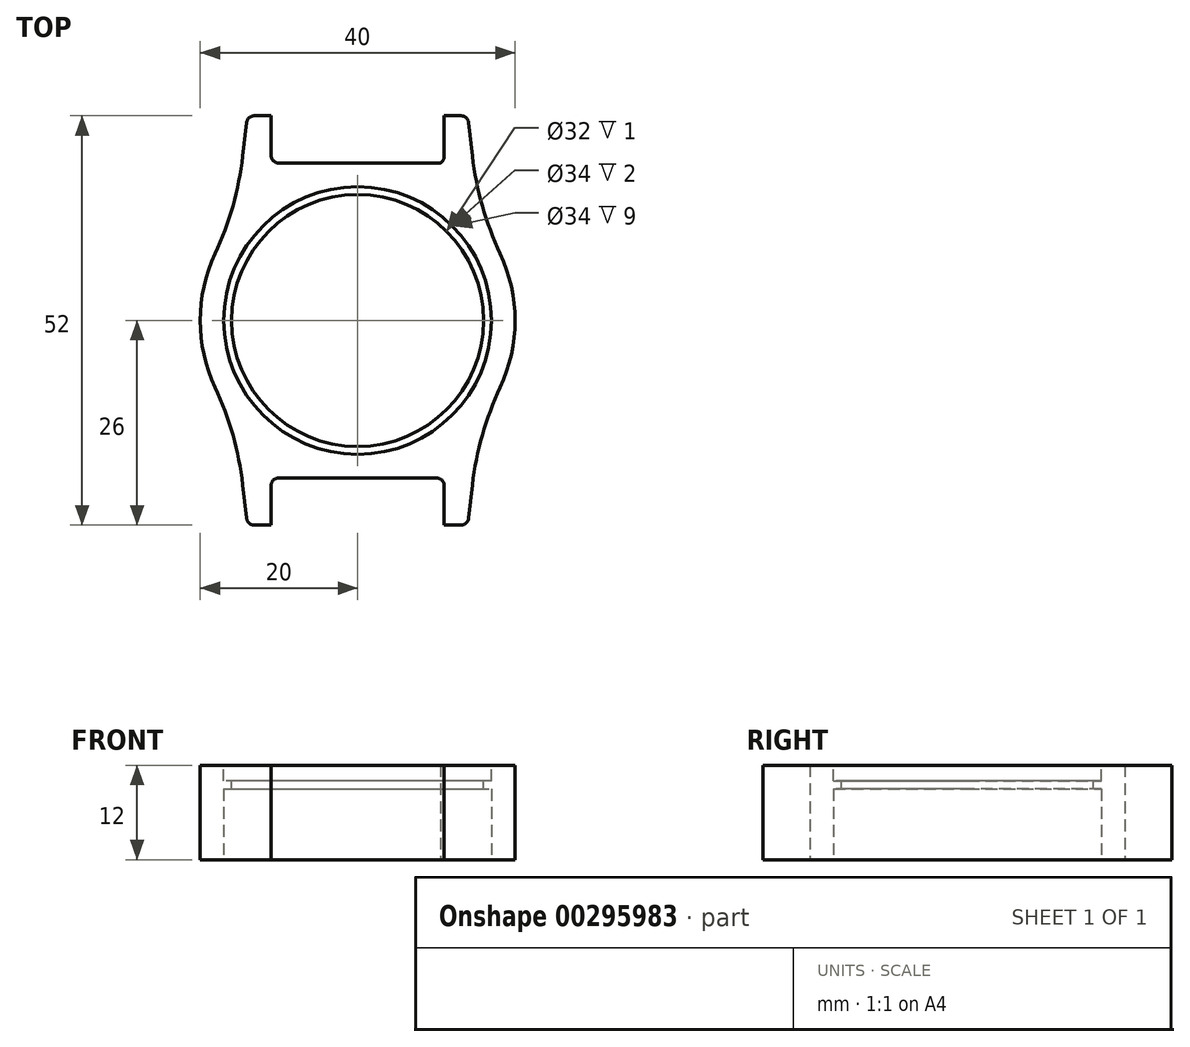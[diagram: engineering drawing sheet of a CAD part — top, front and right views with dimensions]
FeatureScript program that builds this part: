
annotation { "Feature Type Name" : "Feature", "Feature Type Description" : "" }
export const myFeature = defineFeature(function(context is Context, id is Id, definition is map)
    precondition{}
    {
        {
            var Q0;
            Q0=qCreatedBy(makeId("Top.planeOp"),FACE);
            var sketch = newSketch(context, id + "F0", { "sketchPlane" : qUnion([Q0])});
            skLineSegment(sketch, "E0", {"start": v(0, 20) * mm, "end": v(10.54, 20) * mm});
            skLineSegment(sketch, "E1", {"start": v(0, -20) * mm, "end": v(10, -20) * mm});
            skLineSegment(sketch, "E2", {"start": v(0, 20) * mm, "end": v(-10, 20) * mm});
            skLineSegment(sketch, "E3", {"start": v(0, -20) * mm, "end": v(-10, -20) * mm});
            skLineSegment(sketch, "E4", {"start": v(-11, 21) * mm, "end": v(-11, 26) * mm});
            skLineSegment(sketch, "E5", {"start": v(11, 20.84) * mm, "end": v(11, 26) * mm});
            skLineSegment(sketch, "E6", {"start": v(-11, -21) * mm, "end": v(-11, -26) * mm});
            skLineSegment(sketch, "E7", {"start": v(11, -21) * mm, "end": v(11, -26) * mm});
            skLineSegment(sketch, "E8", {"start": v(11, 26) * mm, "end": v(13.1, 26) * mm});
            skLineSegment(sketch, "E9", {"start": v(-11, 26) * mm, "end": v(-13.1, 26) * mm});
            skLineSegment(sketch, "E10", {"start": v(11, -26) * mm, "end": v(13.1, -26) * mm});
            skLineSegment(sketch, "E11", {"start": v(-11, -26) * mm, "end": v(-13.1, -26) * mm});
            skPoint(sketch, "E12.visualSharp", {"position": v(-11, 20) * mm});
            skArc(sketch, "E12.filletArc", {"start": v(-11, 21) * mm, "mid": v(-10.7, 20.3) * mm, "end": v(-10, 20) * mm});
            skPoint(sketch, "E13.visualSharp", {"position": v(11, 20) * mm});
            skArc(sketch, "E13.filletArc", {"start": v(10.54, 20) * mm, "mid": v(10.88, 20.36) * mm, "end": v(11, 20.84) * mm});
            skPoint(sketch, "E14.visualSharp", {"position": v(-11, -20) * mm});
            skArc(sketch, "E14.filletArc", {"start": v(-10, -20) * mm, "mid": v(-10.7, -20.3) * mm, "end": v(-11, -21) * mm});
            skPoint(sketch, "E15.visualSharp", {"position": v(11, -20) * mm});
            skArc(sketch, "E15.filletArc", {"start": v(11, -21) * mm, "mid": v(10.7, -20.3) * mm, "end": v(10, -20) * mm});
            skArc(sketch, "E16", {"start": v(-18.1, 8.49) * mm, "mid": v(-20, 0) * mm, "end": v(-18.1, -8.49) * mm});
            skLineSegment(sketch, "E17", {"start": v(-14.1, -25.11) * mm, "end": v(-14.6, -20.88) * mm});
            skLineSegment(sketch, "E18", {"start": v(14.1, -25.11) * mm, "end": v(14.6, -20.88) * mm});
            skLineSegment(sketch, "E19", {"start": v(-14.1, 25.11) * mm, "end": v(-14.6, 20.88) * mm});
            skLineSegment(sketch, "E20", {"start": v(14.1, 25.11) * mm, "end": v(14.6, 20.88) * mm});
            skArc(sketch, "E21.trimOffspring", {"start": v(18.1, -8.49) * mm, "mid": v(20, 0) * mm, "end": v(18.1, 8.49) * mm});
            skPoint(sketch, "E22.visualSharp", {"position": v(-15.55, -12.58) * mm});
            skArc(sketch, "E22.filletArc", {"start": v(-14.6, -20.88) * mm, "mid": v(-15.85, -14.54) * mm, "end": v(-18.1, -8.49) * mm});
            skPoint(sketch, "E23.visualSharp", {"position": v(15.55, -12.58) * mm});
            skArc(sketch, "E23.filletArc", {"start": v(18.1, -8.49) * mm, "mid": v(15.85, -14.54) * mm, "end": v(14.6, -20.88) * mm});
            skPoint(sketch, "E24.visualSharp", {"position": v(15.55, 12.58) * mm});
            skArc(sketch, "E24.filletArc", {"start": v(14.6, 20.88) * mm, "mid": v(15.85, 14.54) * mm, "end": v(18.1, 8.49) * mm});
            skPoint(sketch, "E25.visualSharp", {"position": v(-15.55, 12.58) * mm});
            skArc(sketch, "E25.filletArc", {"start": v(-18.1, 8.49) * mm, "mid": v(-15.85, 14.54) * mm, "end": v(-14.6, 20.88) * mm});
            skPoint(sketch, "E26.visualSharp", {"position": v(-14, 26) * mm});
            skArc(sketch, "E26.filletArc", {"start": v(-13.1, 26) * mm, "mid": v(-13.77, 25.75) * mm, "end": v(-14.1, 25.11) * mm});
            skPoint(sketch, "E27.visualSharp", {"position": v(14, 26) * mm});
            skArc(sketch, "E27.filletArc", {"start": v(14.1, 25.11) * mm, "mid": v(13.77, 25.75) * mm, "end": v(13.1, 26) * mm});
            skPoint(sketch, "E28.visualSharp", {"position": v(14, -26) * mm});
            skArc(sketch, "E28.filletArc", {"start": v(13.1, -26) * mm, "mid": v(13.77, -25.75) * mm, "end": v(14.1, -25.11) * mm});
            skPoint(sketch, "E29.visualSharp", {"position": v(-14, -26) * mm});
            skArc(sketch, "E29.filletArc", {"start": v(-14.1, -25.11) * mm, "mid": v(-13.77, -25.75) * mm, "end": v(-13.1, -26) * mm});
            skSolve(sketch);
        }
        {
            var Q0;
            Q0=makeQuery(id+"F0.imprint","IMPRINT",FACE,{"disambiguationData":[TD([[makeQuery(id+"F0.imprint","IMPRINT",EDGE,{"derivedFrom":sQuery(id+"F0.wireOp",EDGE,"E0")}),-1.0]])]});
            extrude(context, id + "F1", {"entities" : qUnion([Q0]), "depth" : 12 * mm});
        }
        {
            var Q0;
            Q0=makeQuery(id+"F1.opExtrude","CAP_FACE",FACE,{"disambiguationData":[OSD([sQuery(id+"F0.wireOp",EDGE,"E0"),sQuery(id+"F0.wireOp",EDGE,"E1"),sQuery(id+"F0.wireOp",EDGE,"E2"),sQuery(id+"F0.wireOp",EDGE,"E3"),sQuery(id+"F0.wireOp",EDGE,"E4"),sQuery(id+"F0.wireOp",EDGE,"E5"),sQuery(id+"F0.wireOp",EDGE,"E6"),sQuery(id+"F0.wireOp",EDGE,"E7"),sQuery(id+"F0.wireOp",EDGE,"E8"),sQuery(id+"F0.wireOp",EDGE,"E9"),sQuery(id+"F0.wireOp",EDGE,"E10"),sQuery(id+"F0.wireOp",EDGE,"E11"),sQuery(id+"F0.wireOp",EDGE,"E12.filletArc"),sQuery(id+"F0.wireOp",EDGE,"E13.filletArc"),sQuery(id+"F0.wireOp",EDGE,"E14.filletArc"),sQuery(id+"F0.wireOp",EDGE,"E15.filletArc"),sQuery(id+"F0.wireOp",EDGE,"E16"),sQuery(id+"F0.wireOp",EDGE,"E17"),sQuery(id+"F0.wireOp",EDGE,"E18"),sQuery(id+"F0.wireOp",EDGE,"E19"),sQuery(id+"F0.wireOp",EDGE,"E20"),sQuery(id+"F0.wireOp",EDGE,"E21.trimOffspring"),sQuery(id+"F0.wireOp",EDGE,"E22.filletArc"),sQuery(id+"F0.wireOp",EDGE,"E23.filletArc"),sQuery(id+"F0.wireOp",EDGE,"E24.filletArc"),sQuery(id+"F0.wireOp",EDGE,"E25.filletArc"),sQuery(id+"F0.wireOp",EDGE,"E26.filletArc"),sQuery(id+"F0.wireOp",EDGE,"E27.filletArc"),sQuery(id+"F0.wireOp",EDGE,"E28.filletArc"),sQuery(id+"F0.wireOp",EDGE,"E29.filletArc")])],"isStart":true});
            var sketch = newSketch(context, id + "F2", { "sketchPlane" : qUnion([Q0])});
            skCircle(sketch, "E30", {"center": v(0, 0) * mm, "radius": 17 * mm});
            skSolve(sketch);
        }
        {
            var Q0;
            Q0=makeQuery(id+"F1.opExtrude","CAP_FACE",FACE,{"disambiguationData":[OSD([sQuery(id+"F0.wireOp",EDGE,"E0"),sQuery(id+"F0.wireOp",EDGE,"E1"),sQuery(id+"F0.wireOp",EDGE,"E2"),sQuery(id+"F0.wireOp",EDGE,"E3"),sQuery(id+"F0.wireOp",EDGE,"E4"),sQuery(id+"F0.wireOp",EDGE,"E5"),sQuery(id+"F0.wireOp",EDGE,"E6"),sQuery(id+"F0.wireOp",EDGE,"E7"),sQuery(id+"F0.wireOp",EDGE,"E8"),sQuery(id+"F0.wireOp",EDGE,"E9"),sQuery(id+"F0.wireOp",EDGE,"E10"),sQuery(id+"F0.wireOp",EDGE,"E11"),sQuery(id+"F0.wireOp",EDGE,"E12.filletArc"),sQuery(id+"F0.wireOp",EDGE,"E13.filletArc"),sQuery(id+"F0.wireOp",EDGE,"E14.filletArc"),sQuery(id+"F0.wireOp",EDGE,"E15.filletArc"),sQuery(id+"F0.wireOp",EDGE,"E16"),sQuery(id+"F0.wireOp",EDGE,"E17"),sQuery(id+"F0.wireOp",EDGE,"E18"),sQuery(id+"F0.wireOp",EDGE,"E19"),sQuery(id+"F0.wireOp",EDGE,"E20"),sQuery(id+"F0.wireOp",EDGE,"E21.trimOffspring"),sQuery(id+"F0.wireOp",EDGE,"E22.filletArc"),sQuery(id+"F0.wireOp",EDGE,"E23.filletArc"),sQuery(id+"F0.wireOp",EDGE,"E24.filletArc"),sQuery(id+"F0.wireOp",EDGE,"E25.filletArc"),sQuery(id+"F0.wireOp",EDGE,"E26.filletArc"),sQuery(id+"F0.wireOp",EDGE,"E27.filletArc"),sQuery(id+"F0.wireOp",EDGE,"E28.filletArc"),sQuery(id+"F0.wireOp",EDGE,"E29.filletArc")])],"isStart":false});
            var sketch = newSketch(context, id + "F3", { "sketchPlane" : qUnion([Q0])});
            skCircle(sketch, "E31", {"center": v(0, 0) * mm, "radius": 16 * mm});
            skSolve(sketch);
        }
        {
            var Q0;
            Q0=makeQuery(id+"F3.imprint","IMPRINT",FACE,{"disambiguationData":[TD([[makeQuery(id+"F3.imprint","IMPRINT",EDGE,{"derivedFrom":sQuery(id+"F3.wireOp",EDGE,"E31")}),1.0]])]});
            extrude(context, id + "F4", {"entities" : qUnion([Q0]), "operationType" : NewBodyOperationType.REMOVE, "endBound" : BoundingType.THROUGH_ALL, "oppositeDirection" : true, "depth" : 2 * mm});
        }
        {
            var Q0;
            Q0=makeQuery(id+"F3.imprint","IMPRINT",FACE,{"disambiguationData":[TD([[makeQuery(id+"F3.imprint","IMPRINT",EDGE,{"derivedFrom":sQuery(id+"F3.wireOp",EDGE,"E31")}),-1.0]])]});
            var sketch = newSketch(context, id + "F5", { "sketchPlane" : qUnion([Q0])});
            skCircle(sketch, "E32", {"center": v(0, 0) * mm, "radius": 17 * mm});
            skSolve(sketch);
        }
        {
            var Q0;
            Q0=makeQuery(id+"F5.imprint","IMPRINT",FACE,{"disambiguationData":[TD([[makeQuery(id+"F5.imprint","IMPRINT",EDGE,{"derivedFrom":sQuery(id+"F5.wireOp",EDGE,"E32")}),1.0]])]});
            var Q1;
            Q1=sQuery(id+"F5.wireOp",EDGE,"E32");
            extrude(context, id + "F6", {"entities" : qUnion([Q0]), "operationType" : NewBodyOperationType.REMOVE, "surfaceEntities" : qUnion([Q1]), "oppositeDirection" : true, "depth" : 2 * mm});
        }
        {
            var Q0;
            Q0=makeQuery(id+"F2.imprint","IMPRINT",FACE,{"disambiguationData":[TD([[makeQuery(id+"F2.imprint","IMPRINT",EDGE,{"derivedFrom":sQuery(id+"F2.wireOp",EDGE,"E30")}),1.0]])]});
            extrude(context, id + "F7", {"entities" : qUnion([Q0]), "operationType" : NewBodyOperationType.REMOVE, "oppositeDirection" : true, "depth" : 9 * mm});
        }
        {
            var Q0;
            Q0=qCreatedBy(makeId("Right.planeOp"),FACE);
            var sketch = newSketch(context, id + "F8", { "sketchPlane" : qUnion([Q0])});
            skArc(sketch, "E33", {"start": v(71.6, 0) * mm, "mid": v(-0.24, 11.93) * mm, "end": v(-72.09, 0) * mm});
            skLineSegment(sketch, "E34", {"start": v(-0.24, -210.44) * mm, "end": v(9.76, -210.44) * mm, "construction": true});
            skLineSegment(sketch, "E35", {"start": v(-0.24, -210.44) * mm, "end": v(-10.24, -210.44) * mm, "construction": true});
            skSolve(sketch);
        }
        {
            var Q0;
            Q0=sQuery(id+"F8.wireOp",EDGE,"E33");
            var Q1;
            Q1=sQuery(id+"F8.wireOp",EDGE,"E34");
            revolve(context, id + "F9", {"bodyType" : ToolBodyType.SURFACE, "operationType" : NewBodyOperationType.ADD, "surfaceEntities" : qUnion([Q0]), "axis" : qUnion([Q1]), "revolveType" : RevolveType.SYMMETRIC, "angle" : 30 * degree});
        }
    });
